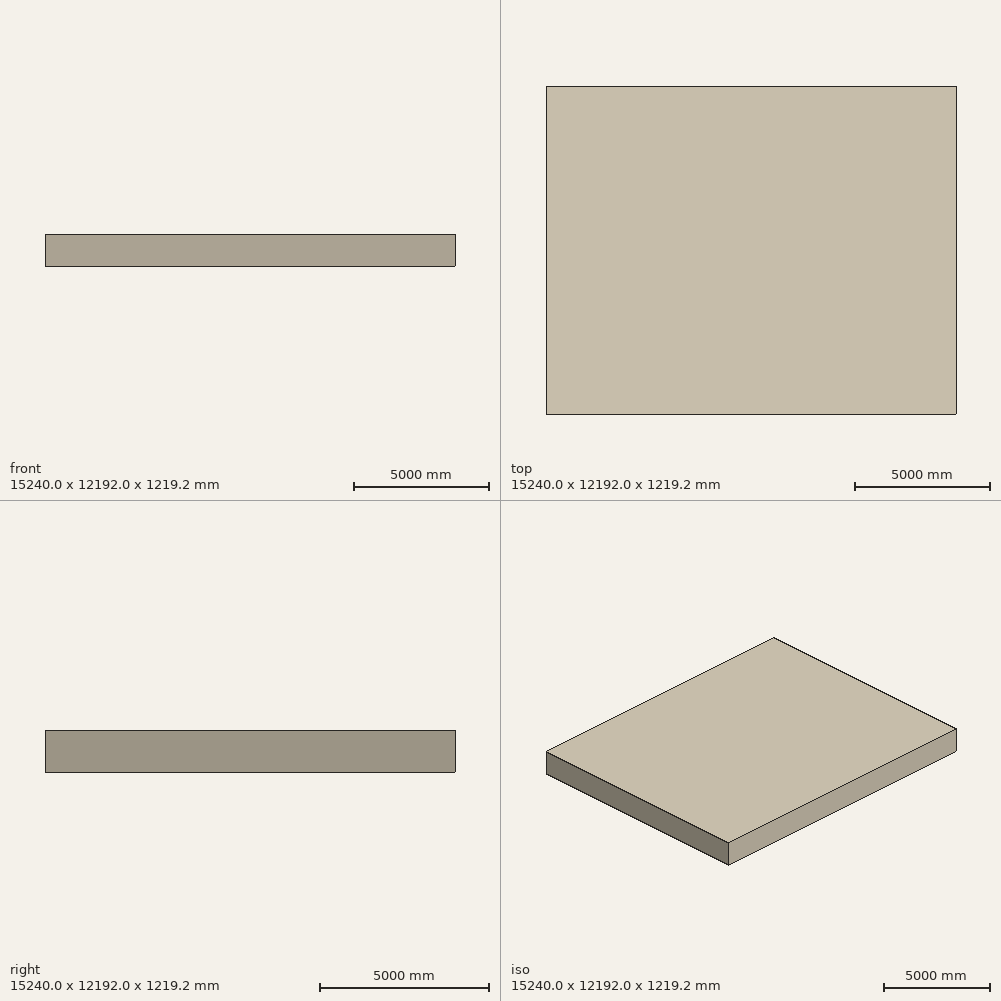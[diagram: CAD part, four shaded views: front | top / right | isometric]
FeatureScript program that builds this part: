
annotation { "Feature Type Name" : "Feature", "Feature Type Description" : "" }
export const myFeature = defineFeature(function(context is Context, id is Id, definition is map)
    precondition{}
    {
        {
            var Q0;
            Q0=qCreatedBy(makeId("Top.planeOp"),FACE);
            var sketch = newSketch(context, id + "F0", { "sketchPlane" : qUnion([Q0])});
            skLineSegment(sketch, "E0.bottom", {"start": v(7620, 6096) * mm, "end": v(-7620, 6096) * mm});
            skLineSegment(sketch, "E0.top", {"start": v(7620, -6096) * mm, "end": v(-7620, -6096) * mm});
            skLineSegment(sketch, "E0.left", {"start": v(7620, 6096) * mm, "end": v(7620, -6096) * mm});
            skLineSegment(sketch, "E0.right", {"start": v(-7620, 6096) * mm, "end": v(-7620, -6096) * mm});
            skPoint(sketch, "E0.middle", {"position": v(0, 0) * mm});
            skSolve(sketch);
        }
        {
            var Q0;
            Q0 = qSketchRegion(id + "F0", true);
            extrude(context, id + "F1", {"entities" : qUnion([Q0]), "oppositeDirection" : true, "depth" : 1219.2 * mm, "offsetDistance" : 25.4 * mm});
        }
    });
